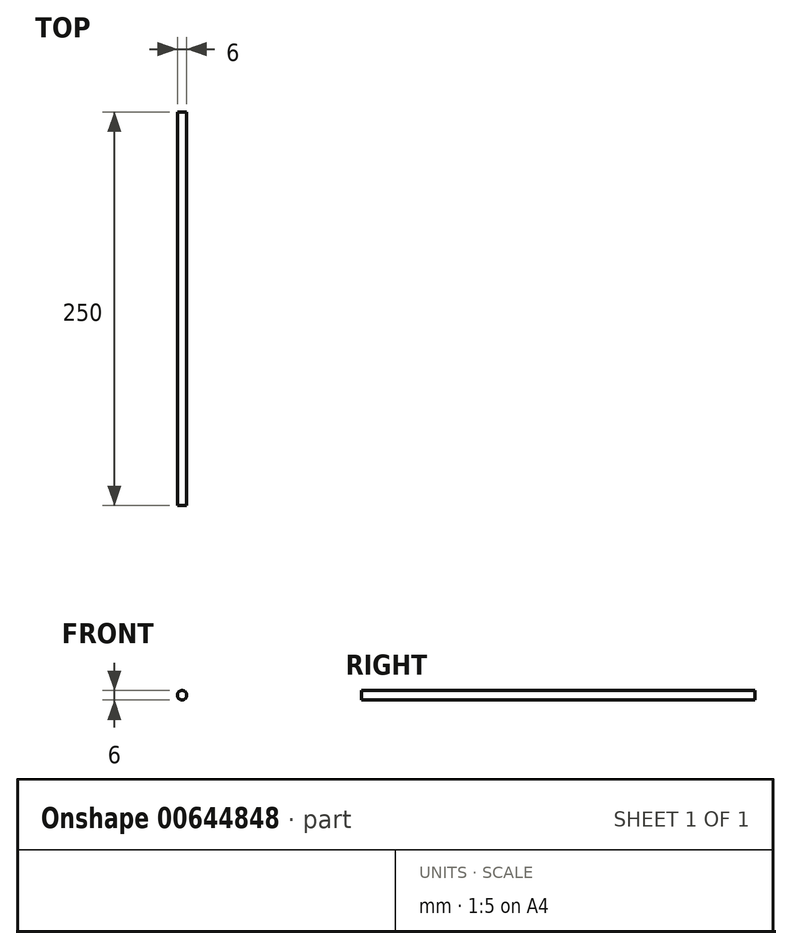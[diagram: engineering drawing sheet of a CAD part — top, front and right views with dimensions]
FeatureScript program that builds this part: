
annotation { "Feature Type Name" : "Feature", "Feature Type Description" : "" }
export const myFeature = defineFeature(function(context is Context, id is Id, definition is map)
    precondition{}
    {
        {
            var Q0;
            Q0=qCreatedBy(makeId("Front.planeOp"),FACE);
            var sketch = newSketch(context, id + "F0", { "sketchPlane" : qUnion([Q0])});
            skCircle(sketch, "E0", {"center": v(0, 0) * mm, "radius": 3 * mm});
            skSolve(sketch);
        }
        {
            var Q0;
            Q0 = qSketchRegion(id + "F0", true);
            extrude(context, id + "F1", {"entities" : qUnion([Q0]), "depth" : 250 * mm, "offsetDistance" : 25 * mm});
        }
    });
